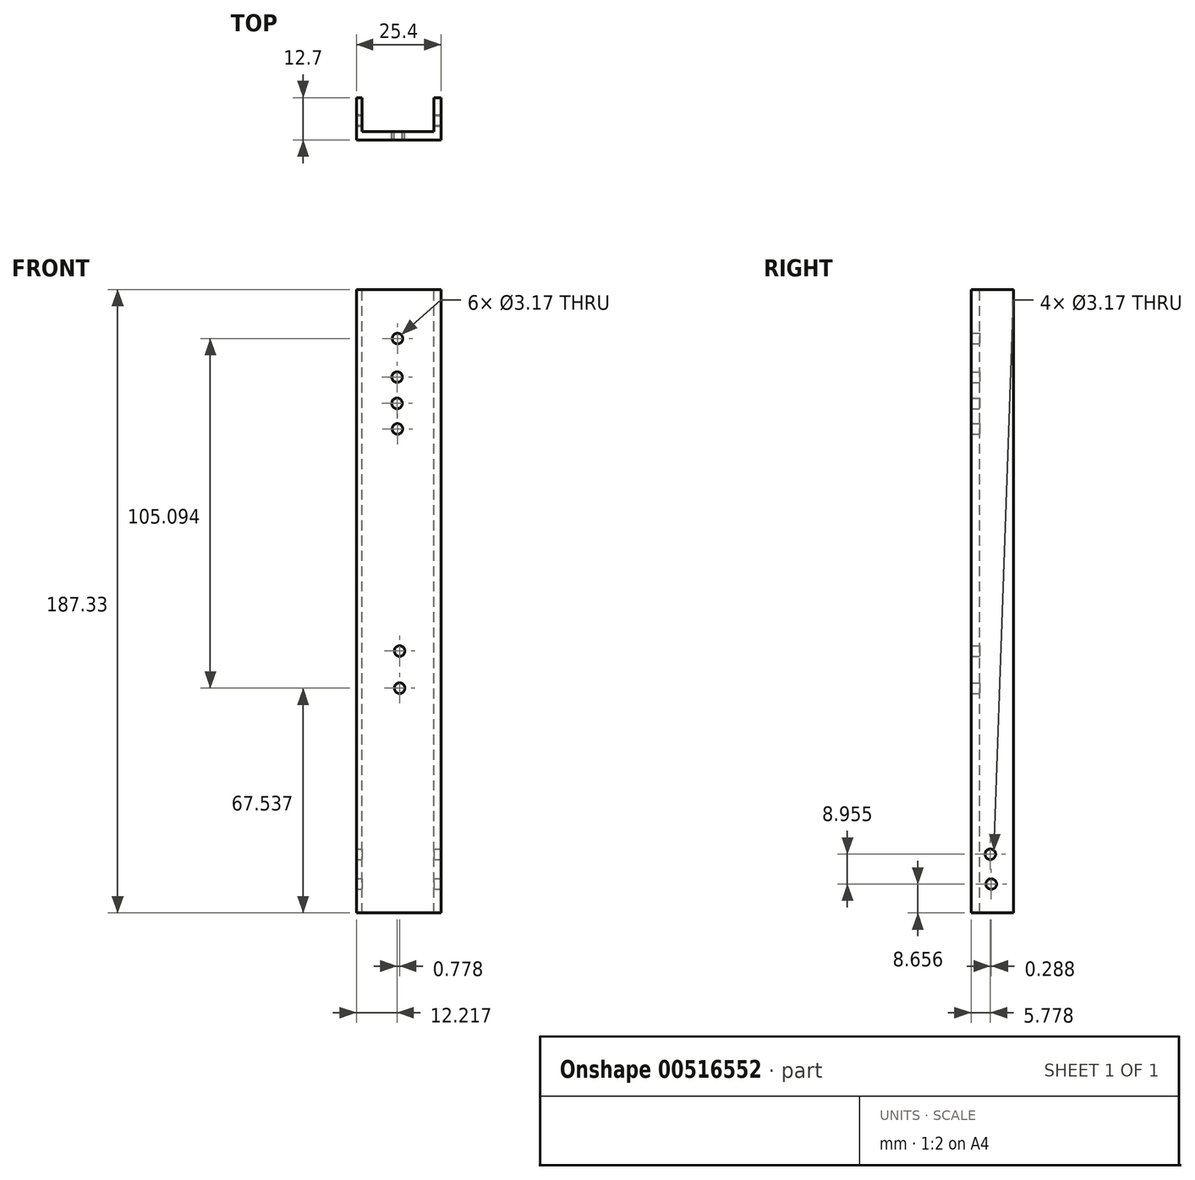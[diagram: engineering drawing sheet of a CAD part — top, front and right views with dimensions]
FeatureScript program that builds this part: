
annotation { "Feature Type Name" : "Feature", "Feature Type Description" : "" }
export const myFeature = defineFeature(function(context is Context, id is Id, definition is map)
    precondition{}
    {
        {
            var Q0;
            Q0=qCreatedBy(makeId("Front.planeOp"),FACE);
            var sketch = newSketch(context, id + "F0", { "sketchPlane" : qUnion([Q0])});
            skLineSegment(sketch, "E0.bottom", {"start": v(-25.4, 54.03) * mm, "end": v(0, 54.03) * mm});
            skLineSegment(sketch, "E0.top", {"start": v(-25.4, -133.3) * mm, "end": v(0, -133.3) * mm});
            skLineSegment(sketch, "E0.left", {"start": v(-25.4, 54.03) * mm, "end": v(-25.4, -133.3) * mm});
            skLineSegment(sketch, "E0.right", {"start": v(0, 54.03) * mm, "end": v(0, -133.3) * mm});
            skSolve(sketch);
        }
        {
            var Q0;
            Q0=makeQuery(id+"F0.imprint","IMPRINT",FACE,{"disambiguationData":[TD([[makeQuery(id+"F0.imprint","IMPRINT",EDGE,{"derivedFrom":sQuery(id+"F0.wireOp",EDGE,"E0.bottom")}),-1.0]])]});
            extrude(context, id + "F1", {"entities" : qUnion([Q0]), "depth" : 12.7 * mm, "offsetDistance" : 25.4 * mm});
        }
        {
            var Q0;
            Q0=qCreatedBy(makeId("Front.planeOp"),FACE);
            var sketch = newSketch(context, id + "F2", { "sketchPlane" : qUnion([Q0])});
            skLineSegment(sketch, "E1.bottom", {"start": v(-2.13, -141.73) * mm, "end": v(-23.72, -141.73) * mm});
            skLineSegment(sketch, "E1.top", {"start": v(-2.13, 61.47) * mm, "end": v(-23.72, 61.47) * mm});
            skLineSegment(sketch, "E1.left", {"start": v(-2.13, -141.73) * mm, "end": v(-2.13, 61.47) * mm});
            skLineSegment(sketch, "E1.right", {"start": v(-23.72, -141.73) * mm, "end": v(-23.72, 61.47) * mm});
            skSolve(sketch);
        }
        {
            var Q0;
            Q0=makeQuery(id+"F2.imprint","IMPRINT",FACE,{"disambiguationData":[TD([[makeQuery(id+"F2.imprint","IMPRINT",EDGE,{"derivedFrom":sQuery(id+"F2.wireOp",EDGE,"E1.bottom")}),-1.0]])]});
            extrude(context, id + "F3", {"entities" : qUnion([Q0]), "operationType" : NewBodyOperationType.REMOVE, "depth" : 10.16 * mm, "offsetDistance" : 25.4 * mm});
        }
        {
            var Q0;
            Q0=makeQuery(id+"F1.opExtrude","SWEPT_FACE",FACE,{"disambiguationData":[OSD([sQuery(id+"F0.wireOp",EDGE,"E0.right")])]});
            var sketch = newSketch(context, id + "F4", { "sketchPlane" : qUnion([Q0])});
            skCircle(sketch, "E2", {"center": v(-6.63, -124.64) * mm, "radius": 1.65 * mm});
            skSolve(sketch);
        }
        {
            var Q0;
            Q0=sQuery(id+"F4.wireOp",VERTEX,"E2.center");
            var Q1;
            Q1=makeQuery(id+"F1.opExtrude","SWEPT_BODY",BODY,{"disambiguationData":[OSD([sQuery(id+"F0.wireOp",EDGE,"E0.bottom"),sQuery(id+"F0.wireOp",EDGE,"E0.top"),sQuery(id+"F0.wireOp",EDGE,"E0.left"),sQuery(id+"F0.wireOp",EDGE,"E0.right")])]});
            hole(context, id + "F5", {"style" : HoleStyle.SIMPLE, "endStyle" : HoleEndStyle.THROUGH, "holeDiameter" : 3.17 * mm, "isTappedThrough" : true, "tappedDepth" : 12.7 * mm, "tapClearance" : 3, "locations" : qUnion([Q0]), "scope" : qUnion([Q1])});
        }
        {
            var Q0;
            Q0=makeQuery(id+"F1.opExtrude","SWEPT_FACE",FACE,{"disambiguationData":[OSD([sQuery(id+"F0.wireOp",EDGE,"E0.right")])]});
            var sketch = newSketch(context, id + "F6", { "sketchPlane" : qUnion([Q0])});
            skCircle(sketch, "E3", {"center": v(-6.92, -115.69) * mm, "radius": 1.67 * mm});
            skSolve(sketch);
        }
        {
            var Q0;
            Q0=sQuery(id+"F6.wireOp",VERTEX,"E3.center");
            var Q1;
            Q1=makeQuery(id+"F1.opExtrude","SWEPT_BODY",BODY,{"disambiguationData":[OSD([sQuery(id+"F0.wireOp",EDGE,"E0.bottom"),sQuery(id+"F0.wireOp",EDGE,"E0.top"),sQuery(id+"F0.wireOp",EDGE,"E0.left"),sQuery(id+"F0.wireOp",EDGE,"E0.right")])]});
            hole(context, id + "F7", {"style" : HoleStyle.SIMPLE, "endStyle" : HoleEndStyle.THROUGH, "holeDiameter" : 3.17 * mm, "isTappedThrough" : true, "tappedDepth" : 12.7 * mm, "tapClearance" : 3, "locations" : qUnion([Q0]), "scope" : qUnion([Q1])});
        }
        {
            var Q0;
            Q0=makeQuery(id+"F3.boolean.opBoolean","COPY",FACE,{"derivedFrom":makeQuery(id+"F3.opExtrude","CAP_FACE",FACE,{"disambiguationData":[OSD([sQuery(id+"F2.wireOp",EDGE,"E1.bottom"),sQuery(id+"F2.wireOp",EDGE,"E1.top"),sQuery(id+"F2.wireOp",EDGE,"E1.left"),sQuery(id+"F2.wireOp",EDGE,"E1.right")])],"isStart":false})});
            var sketch = newSketch(context, id + "F8", { "sketchPlane" : qUnion([Q0])});
            skCircle(sketch, "E4", {"center": v(13.04, 39.33) * mm, "radius": 1.66 * mm});
            skSolve(sketch);
        }
        {
            var Q0;
            Q0=sQuery(id+"F8.wireOp",VERTEX,"E4.center");
            var Q1;
            Q1=makeQuery(id+"F1.opExtrude","SWEPT_BODY",BODY,{"disambiguationData":[OSD([sQuery(id+"F0.wireOp",EDGE,"E0.bottom"),sQuery(id+"F0.wireOp",EDGE,"E0.top"),sQuery(id+"F0.wireOp",EDGE,"E0.left"),sQuery(id+"F0.wireOp",EDGE,"E0.right")])]});
            hole(context, id + "F9", {"style" : HoleStyle.SIMPLE, "endStyle" : HoleEndStyle.THROUGH, "holeDiameter" : 3.17 * mm, "isTappedThrough" : true, "tappedDepth" : 12.7 * mm, "tapClearance" : 3, "locations" : qUnion([Q0]), "scope" : qUnion([Q1])});
        }
        {
            var Q0;
            Q0=makeQuery(id+"F3.boolean.opBoolean","COPY",FACE,{"derivedFrom":makeQuery(id+"F3.opExtrude","CAP_FACE",FACE,{"disambiguationData":[OSD([sQuery(id+"F2.wireOp",EDGE,"E1.bottom"),sQuery(id+"F2.wireOp",EDGE,"E1.top"),sQuery(id+"F2.wireOp",EDGE,"E1.left"),sQuery(id+"F2.wireOp",EDGE,"E1.right")])],"isStart":false})});
            var sketch = newSketch(context, id + "F10", { "sketchPlane" : qUnion([Q0])});
            skCircle(sketch, "E5", {"center": v(13.17, 27.75) * mm, "radius": 1.62 * mm});
            skSolve(sketch);
        }
        {
            var Q0;
            Q0=sQuery(id+"F10.wireOp",VERTEX,"E5.center");
            var Q1;
            Q1=makeQuery(id+"F1.opExtrude","SWEPT_BODY",BODY,{"disambiguationData":[OSD([sQuery(id+"F0.wireOp",EDGE,"E0.bottom"),sQuery(id+"F0.wireOp",EDGE,"E0.top"),sQuery(id+"F0.wireOp",EDGE,"E0.left"),sQuery(id+"F0.wireOp",EDGE,"E0.right")])]});
            hole(context, id + "F11", {"style" : HoleStyle.SIMPLE, "endStyle" : HoleEndStyle.THROUGH, "holeDiameter" : 3.17 * mm, "isTappedThrough" : true, "tappedDepth" : 12.7 * mm, "tapClearance" : 3, "locations" : qUnion([Q0]), "scope" : qUnion([Q1])});
        }
        {
            var Q0;
            Q0=makeQuery(id+"F3.boolean.opBoolean","COPY",FACE,{"derivedFrom":makeQuery(id+"F3.opExtrude","CAP_FACE",FACE,{"disambiguationData":[OSD([sQuery(id+"F2.wireOp",EDGE,"E1.bottom"),sQuery(id+"F2.wireOp",EDGE,"E1.top"),sQuery(id+"F2.wireOp",EDGE,"E1.left"),sQuery(id+"F2.wireOp",EDGE,"E1.right")])],"isStart":false})});
            var sketch = newSketch(context, id + "F12", { "sketchPlane" : qUnion([Q0])});
            skCircle(sketch, "E6", {"center": v(13.18, 19.84) * mm, "radius": 2.05 * mm});
            skSolve(sketch);
        }
        {
            var Q0;
            Q0=sQuery(id+"F12.wireOp",VERTEX,"E6.center");
            var Q1;
            Q1=makeQuery(id+"F1.opExtrude","SWEPT_BODY",BODY,{"disambiguationData":[OSD([sQuery(id+"F0.wireOp",EDGE,"E0.bottom"),sQuery(id+"F0.wireOp",EDGE,"E0.top"),sQuery(id+"F0.wireOp",EDGE,"E0.left"),sQuery(id+"F0.wireOp",EDGE,"E0.right")])]});
            hole(context, id + "F13", {"style" : HoleStyle.SIMPLE, "endStyle" : HoleEndStyle.THROUGH, "holeDiameter" : 3.17 * mm, "isTappedThrough" : true, "tappedDepth" : 12.7 * mm, "tapClearance" : 3, "locations" : qUnion([Q0]), "scope" : qUnion([Q1])});
        }
        {
            var Q0;
            Q0=makeQuery(id+"F3.boolean.opBoolean","COPY",FACE,{"derivedFrom":makeQuery(id+"F3.opExtrude","CAP_FACE",FACE,{"disambiguationData":[OSD([sQuery(id+"F2.wireOp",EDGE,"E1.bottom"),sQuery(id+"F2.wireOp",EDGE,"E1.top"),sQuery(id+"F2.wireOp",EDGE,"E1.left"),sQuery(id+"F2.wireOp",EDGE,"E1.right")])],"isStart":false})});
            var sketch = newSketch(context, id + "F14", { "sketchPlane" : qUnion([Q0])});
            skCircle(sketch, "E7", {"center": v(13.06, 12.18) * mm, "radius": 2.34 * mm});
            skSolve(sketch);
        }
        {
            var Q0;
            Q0=sQuery(id+"F14.wireOp",VERTEX,"E7.center");
            var Q1;
            Q1=makeQuery(id+"F1.opExtrude","SWEPT_BODY",BODY,{"disambiguationData":[OSD([sQuery(id+"F0.wireOp",EDGE,"E0.bottom"),sQuery(id+"F0.wireOp",EDGE,"E0.top"),sQuery(id+"F0.wireOp",EDGE,"E0.left"),sQuery(id+"F0.wireOp",EDGE,"E0.right")])]});
            hole(context, id + "F15", {"style" : HoleStyle.SIMPLE, "endStyle" : HoleEndStyle.THROUGH, "holeDiameter" : 3.17 * mm, "isTappedThrough" : true, "tappedDepth" : 12.7 * mm, "tapClearance" : 3, "locations" : qUnion([Q0]), "scope" : qUnion([Q1])});
        }
        {
            var Q0;
            Q0=makeQuery(id+"F3.boolean.opBoolean","COPY",FACE,{"derivedFrom":makeQuery(id+"F3.opExtrude","CAP_FACE",FACE,{"disambiguationData":[OSD([sQuery(id+"F2.wireOp",EDGE,"E1.bottom"),sQuery(id+"F2.wireOp",EDGE,"E1.top"),sQuery(id+"F2.wireOp",EDGE,"E1.left"),sQuery(id+"F2.wireOp",EDGE,"E1.right")])],"isStart":false})});
            var sketch = newSketch(context, id + "F16", { "sketchPlane" : qUnion([Q0])});
            skCircle(sketch, "E8", {"center": v(12.4, -54.6) * mm, "radius": 2.62 * mm});
            skSolve(sketch);
        }
        {
            var Q0;
            Q0=sQuery(id+"F16.wireOp",VERTEX,"E8.center");
            var Q1;
            Q1=makeQuery(id+"F1.opExtrude","SWEPT_BODY",BODY,{"disambiguationData":[OSD([sQuery(id+"F0.wireOp",EDGE,"E0.bottom"),sQuery(id+"F0.wireOp",EDGE,"E0.top"),sQuery(id+"F0.wireOp",EDGE,"E0.left"),sQuery(id+"F0.wireOp",EDGE,"E0.right")])]});
            hole(context, id + "F17", {"style" : HoleStyle.SIMPLE, "endStyle" : HoleEndStyle.THROUGH, "holeDiameter" : 3.17 * mm, "isTappedThrough" : true, "tappedDepth" : 12.7 * mm, "tapClearance" : 3, "locations" : qUnion([Q0]), "scope" : qUnion([Q1])});
        }
        {
            var Q0;
            Q0=makeQuery(id+"F3.boolean.opBoolean","COPY",FACE,{"derivedFrom":makeQuery(id+"F3.opExtrude","CAP_FACE",FACE,{"disambiguationData":[OSD([sQuery(id+"F2.wireOp",EDGE,"E1.bottom"),sQuery(id+"F2.wireOp",EDGE,"E1.top"),sQuery(id+"F2.wireOp",EDGE,"E1.left"),sQuery(id+"F2.wireOp",EDGE,"E1.right")])],"isStart":false})});
            var sketch = newSketch(context, id + "F18", { "sketchPlane" : qUnion([Q0])});
            skCircle(sketch, "E9", {"center": v(12.4, -65.76) * mm, "radius": 3.15 * mm});
            skSolve(sketch);
        }
        {
            var Q0;
            Q0=sQuery(id+"F18.wireOp",VERTEX,"E9.center");
            var Q1;
            Q1=makeQuery(id+"F1.opExtrude","SWEPT_BODY",BODY,{"disambiguationData":[OSD([sQuery(id+"F0.wireOp",EDGE,"E0.bottom"),sQuery(id+"F0.wireOp",EDGE,"E0.top"),sQuery(id+"F0.wireOp",EDGE,"E0.left"),sQuery(id+"F0.wireOp",EDGE,"E0.right")])]});
            hole(context, id + "F19", {"style" : HoleStyle.SIMPLE, "endStyle" : HoleEndStyle.THROUGH, "holeDiameter" : 3.17 * mm, "isTappedThrough" : true, "tappedDepth" : 12.7 * mm, "tapClearance" : 3, "locations" : qUnion([Q0]), "scope" : qUnion([Q1])});
        }
    });
